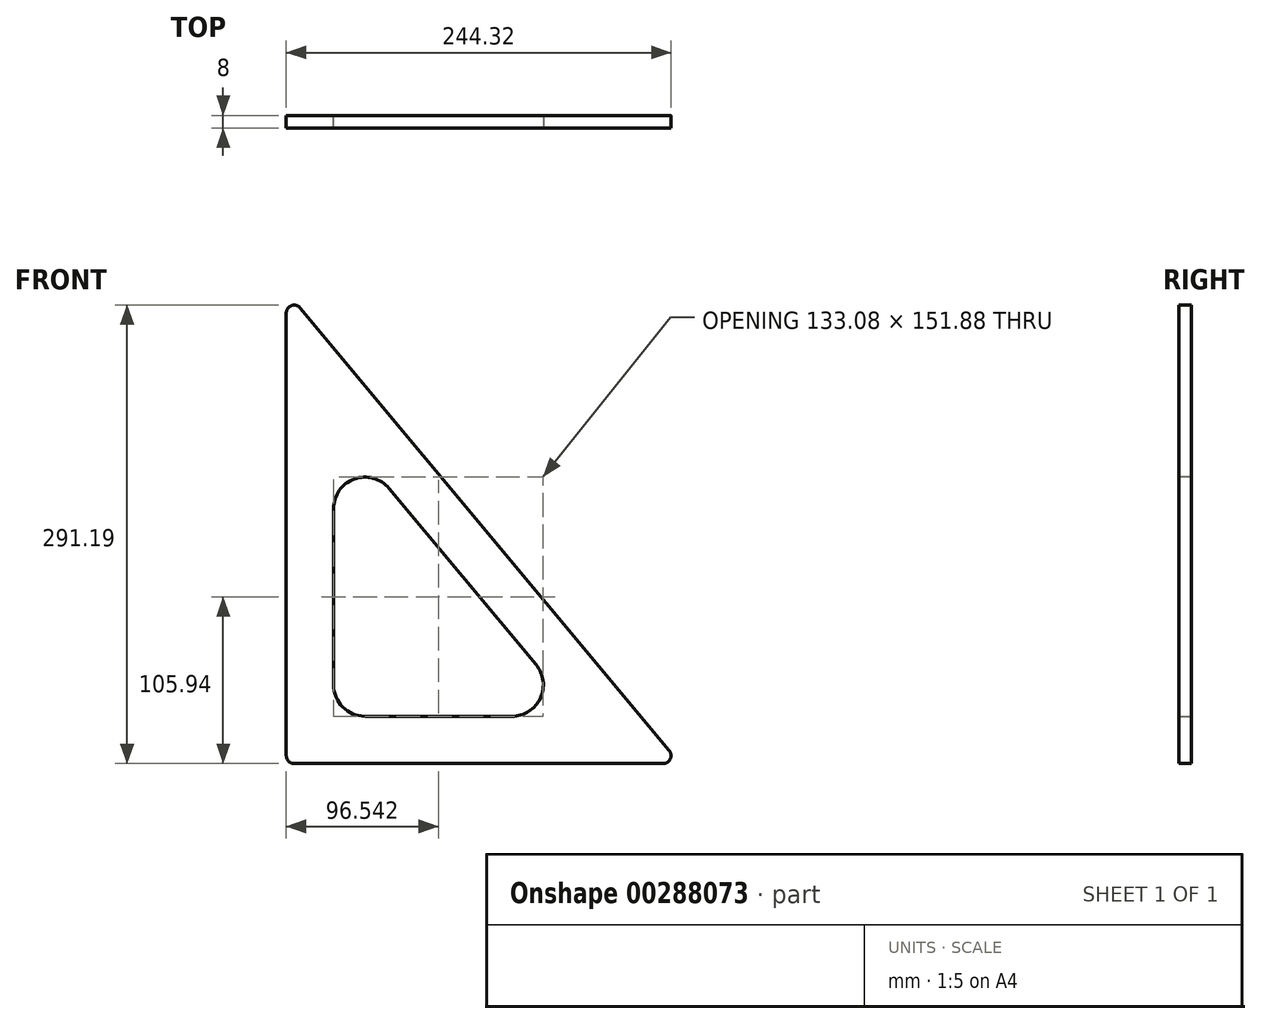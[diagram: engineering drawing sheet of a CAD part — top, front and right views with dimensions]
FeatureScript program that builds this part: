
annotation { "Feature Type Name" : "Feature", "Feature Type Description" : "" }
export const myFeature = defineFeature(function(context is Context, id is Id, definition is map)
    precondition{}
    {
        {
            var Q0;
            Q0=qCreatedBy(makeId("Front.planeOp"),FACE);
            var sketch = newSketch(context, id + "F0", { "sketchPlane" : qUnion([Q0])});
            skLineSegment(sketch, "E0", {"start": v(0, 300) * mm, "end": v(0, 0) * mm});
            skLineSegment(sketch, "E1", {"start": v(0, 0) * mm, "end": v(250, 0) * mm});
            skLineSegment(sketch, "E2", {"start": v(250, 0) * mm, "end": v(0, 300) * mm});
            skLineSegment(sketch, "E3.0", {"start": v(30, 217.14) * mm, "end": v(30, 30) * mm});
            skLineSegment(sketch, "E3.1", {"start": v(185.95, 30) * mm, "end": v(30, 217.14) * mm});
            skLineSegment(sketch, "E3.2", {"start": v(30, 30) * mm, "end": v(185.95, 30) * mm});
            skSolve(sketch);
        }
        {
            var Q0;
            Q0=makeQuery(id+"F0.imprint","IMPRINT",FACE,{"disambiguationData":[TD([[makeQuery(id+"F0.imprint","IMPRINT",EDGE,{"derivedFrom":sQuery(id+"F0.wireOp",EDGE,"E0")}),1.0]])]});
            extrude(context, id + "F1", {"entities" : qUnion([Q0]), "depth" : 8 * mm});
        }
        {
            var Q0;
            Q0=makeQuery(id+"F1.opExtrude","SWEPT_EDGE",EDGE,{"disambiguationData":[OSD([sQuery(id+"F0.wireOp",EDGE,"E3.0"),sQuery(id+"F0.wireOp",EDGE,"E3.2")])]});
            var Q1;
            Q1=makeQuery(id+"F1.opExtrude","SWEPT_EDGE",EDGE,{"disambiguationData":[OSD([sQuery(id+"F0.wireOp",EDGE,"E3.1"),sQuery(id+"F0.wireOp",EDGE,"E3.2")])]});
            var Q2;
            Q2=makeQuery(id+"F1.opExtrude","SWEPT_EDGE",EDGE,{"disambiguationData":[OSD([sQuery(id+"F0.wireOp",EDGE,"E3.0"),sQuery(id+"F0.wireOp",EDGE,"E3.1")])]});
            fillet(context, id + "F2", {"entities" : qUnion([Q0, Q1, Q2]), "radius" : 20 * mm, "tangentPropagation" : true, "allowEdgeOverflow" : false});
        }
        {
            var Q0;
            Q0=makeQuery(id+"F1.opExtrude","SWEPT_EDGE",EDGE,{"disambiguationData":[OSD([sQuery(id+"F0.wireOp",EDGE,"E1"),sQuery(id+"F0.wireOp",EDGE,"E2")])]});
            var Q1;
            Q1=makeQuery(id+"F1.opExtrude","SWEPT_EDGE",EDGE,{"disambiguationData":[OSD([sQuery(id+"F0.wireOp",EDGE,"E0"),sQuery(id+"F0.wireOp",EDGE,"E2")])]});
            var Q2;
            Q2=makeQuery(id+"F1.opExtrude","SWEPT_EDGE",EDGE,{"disambiguationData":[OSD([sQuery(id+"F0.wireOp",EDGE,"E0"),sQuery(id+"F0.wireOp",EDGE,"E1")])]});
            fillet(context, id + "F3", {"entities" : qUnion([Q0, Q1, Q2]), "radius" : 5 * mm, "tangentPropagation" : true, "allowEdgeOverflow" : false});
        }
    });
